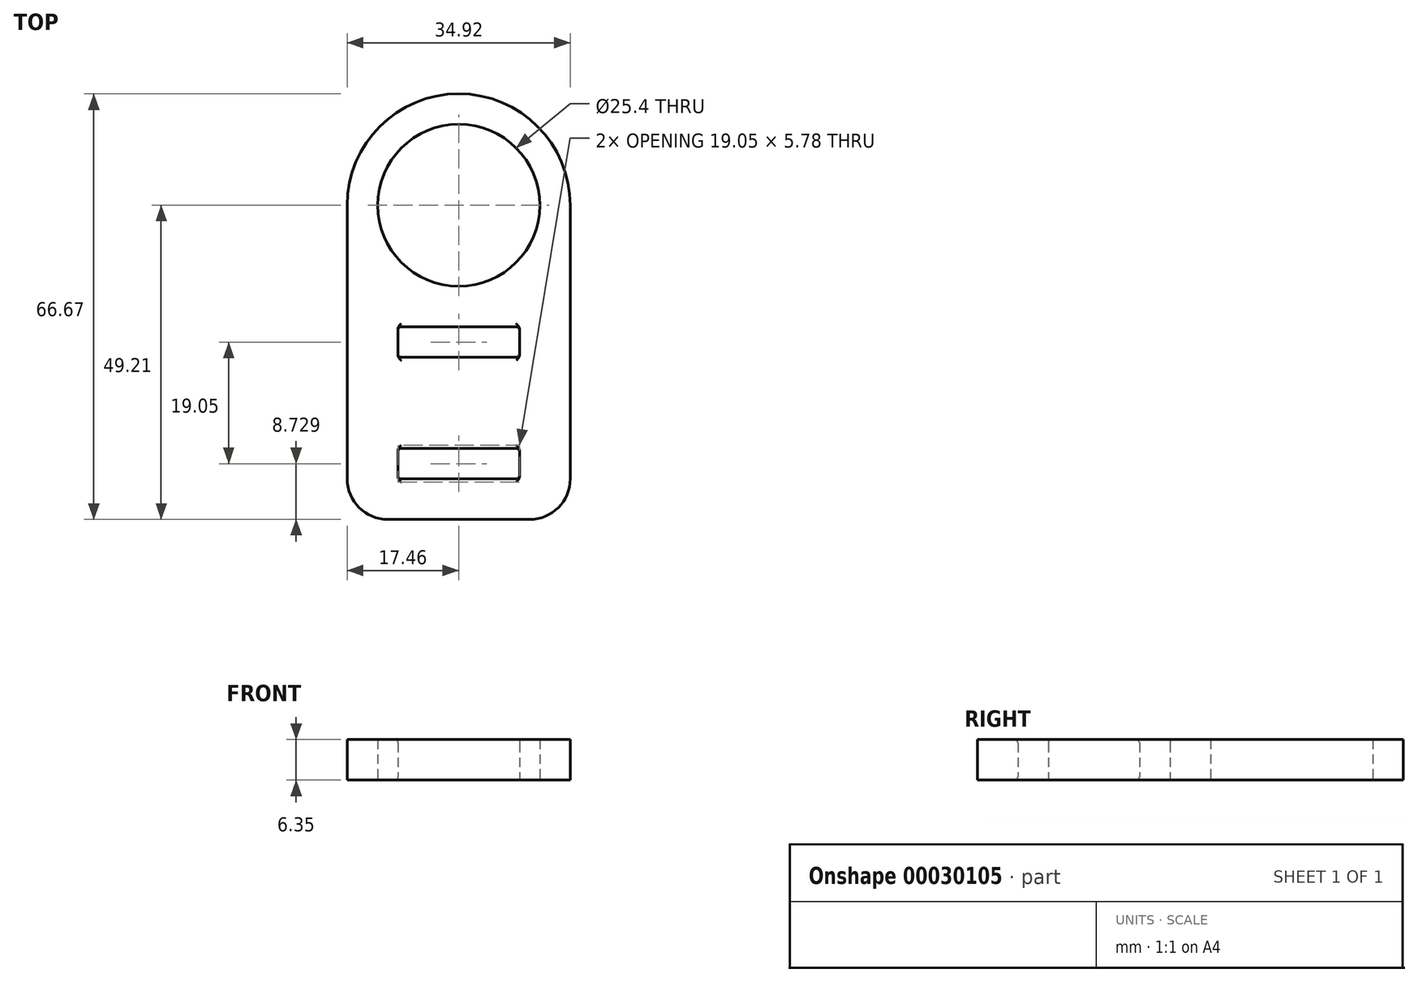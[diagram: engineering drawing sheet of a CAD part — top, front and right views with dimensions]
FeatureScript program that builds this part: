
annotation { "Feature Type Name" : "Feature", "Feature Type Description" : "" }
export const myFeature = defineFeature(function(context is Context, id is Id, definition is map)
    precondition{}
    {
        {
            var Q0;
            Q0=qCreatedBy(makeId("Top.planeOp"),FACE);
            var sketch = newSketch(context, id + "F0", { "sketchPlane" : qUnion([Q0])});
            skCircle(sketch, "E0", {"center": v(0, 0) * mm, "radius": 12.7 * mm});
            skArc(sketch, "E1", {"start": v(17.46, 0) * mm, "mid": v(0, 17.46) * mm, "end": v(-17.46, 0) * mm});
            skLineSegment(sketch, "E2", {"start": v(-17.46, 0) * mm, "end": v(-17.46, -42.86) * mm});
            skLineSegment(sketch, "E3", {"start": v(17.46, 0) * mm, "end": v(17.46, -42.86) * mm});
            skLineSegment(sketch, "E4", {"start": v(11.11, -49.21) * mm, "end": v(-11.11, -49.21) * mm});
            skLineSegment(sketch, "E5", {"start": v(0, 17.46) * mm, "end": v(0, -49.21) * mm, "construction": true});
            skPoint(sketch, "E6.visualSharp", {"position": v(-17.46, -49.21) * mm});
            skArc(sketch, "E6.filletArc", {"start": v(-17.46, -42.86) * mm, "mid": v(-15.6, -47.35) * mm, "end": v(-11.11, -49.21) * mm});
            skPoint(sketch, "E7.visualSharp", {"position": v(17.46, -49.21) * mm});
            skArc(sketch, "E7.filletArc", {"start": v(11.11, -49.21) * mm, "mid": v(15.6, -47.35) * mm, "end": v(17.46, -42.86) * mm});
            skLineSegment(sketch, "E8.rect.bottom", {"start": v(9.53, -38.1) * mm, "end": v(-9.52, -38.1) * mm});
            skLineSegment(sketch, "E8.rect.top", {"start": v(9.53, -42.86) * mm, "end": v(-9.52, -42.86) * mm});
            skLineSegment(sketch, "E8.rect.left", {"start": v(9.53, -38.1) * mm, "end": v(9.53, -42.86) * mm});
            skLineSegment(sketch, "E8.rect.right", {"start": v(-9.52, -38.1) * mm, "end": v(-9.52, -42.86) * mm});
            skPoint(sketch, "E8.rect.middle", {"position": v(0, -40.48) * mm});
            skLineSegment(sketch, "E9.0.1.0", {"start": v(9.53, -23.81) * mm, "end": v(-9.52, -23.81) * mm});
            skLineSegment(sketch, "E9.0.1.1", {"start": v(-9.52, -19.05) * mm, "end": v(-9.52, -23.81) * mm});
            skLineSegment(sketch, "E9.0.1.2", {"start": v(9.53, -19.05) * mm, "end": v(-9.52, -19.05) * mm});
            skLineSegment(sketch, "E9.0.1.3", {"start": v(9.53, -19.05) * mm, "end": v(9.53, -23.81) * mm});
            skLineSegment(sketch, "E9.direction1", {"start": v(-9.52, -42.86) * mm, "end": v(53.5, -42.86) * mm, "construction": true});
            skLineSegment(sketch, "E9.direction2", {"start": v(-9.52, -42.86) * mm, "end": v(-9.52, -23.81) * mm, "construction": true});
            skSolve(sketch);
        }
        {
            var Q0;
            Q0 = qSketchRegion(id + "F0", true);
            extrude(context, id + "F1", {"entities" : qUnion([Q0]), "depth" : 6.35 * mm});
        }
        {
            var Q0;
            Q0=makeQuery(id+"F1.opExtrude","CAP_EDGE",EDGE,{"disambiguationData":[OSD([sQuery(id+"F0.wireOp",EDGE,"E9.0.1.0")])],"isStart":false});
            var Q1;
            Q1=makeQuery(id+"F1.opExtrude","CAP_EDGE",EDGE,{"disambiguationData":[OSD([sQuery(id+"F0.wireOp",EDGE,"E9.0.1.0")])],"isStart":true});
            var Q2;
            Q2=makeQuery(id+"F1.opExtrude","CAP_EDGE",EDGE,{"disambiguationData":[OSD([sQuery(id+"F0.wireOp",EDGE,"E9.0.1.2")])],"isStart":false});
            var Q3;
            Q3=makeQuery(id+"F1.opExtrude","CAP_EDGE",EDGE,{"disambiguationData":[OSD([sQuery(id+"F0.wireOp",EDGE,"E8.rect.bottom")])],"isStart":false});
            var Q4;
            Q4=makeQuery(id+"F1.opExtrude","CAP_EDGE",EDGE,{"disambiguationData":[OSD([sQuery(id+"F0.wireOp",EDGE,"E8.rect.top")])],"isStart":false});
            var Q5;
            Q5=makeQuery(id+"F1.opExtrude","CAP_EDGE",EDGE,{"disambiguationData":[OSD([sQuery(id+"F0.wireOp",EDGE,"E8.rect.bottom")])],"isStart":true});
            var Q6;
            Q6=makeQuery(id+"F1.opExtrude","CAP_EDGE",EDGE,{"disambiguationData":[OSD([sQuery(id+"F0.wireOp",EDGE,"E9.0.1.2")])],"isStart":true});
            var Q7;
            Q7=makeQuery(id+"F1.opExtrude","CAP_EDGE",EDGE,{"disambiguationData":[OSD([sQuery(id+"F0.wireOp",EDGE,"E8.rect.top")])],"isStart":true});
            fillet(context, id + "F2", {"entities" : qUnion([Q0, Q1, Q2, Q3, Q4, Q5, Q6, Q7]), "radius" : 0.5 * mm, "tangentPropagation" : true, "allowEdgeOverflow" : false});
        }
        {
            var Q0;
            Q0=makeQuery(id+"F1.opExtrude","SWEPT_EDGE",EDGE,{"disambiguationData":[OSD([sQuery(id+"F0.wireOp",EDGE,"E8.rect.top"),sQuery(id+"F0.wireOp",EDGE,"E8.rect.left")])]});
            var Q1;
            Q1=makeQuery(id+"F1.opExtrude","SWEPT_EDGE",EDGE,{"disambiguationData":[OSD([sQuery(id+"F0.wireOp",EDGE,"E9.0.1.0"),sQuery(id+"F0.wireOp",EDGE,"E9.0.1.3")])]});
            var Q2;
            Q2=makeQuery(id+"F1.opExtrude","SWEPT_EDGE",EDGE,{"disambiguationData":[OSD([sQuery(id+"F0.wireOp",EDGE,"E8.rect.top"),sQuery(id+"F0.wireOp",EDGE,"E8.rect.right")])]});
            var Q3;
            Q3=makeQuery(id+"F1.opExtrude","SWEPT_EDGE",EDGE,{"disambiguationData":[OSD([sQuery(id+"F0.wireOp",EDGE,"E9.0.1.2"),sQuery(id+"F0.wireOp",EDGE,"E9.0.1.3")])]});
            var Q4;
            Q4=makeQuery(id+"F1.opExtrude","SWEPT_EDGE",EDGE,{"disambiguationData":[OSD([sQuery(id+"F0.wireOp",EDGE,"E9.0.1.1"),sQuery(id+"F0.wireOp",EDGE,"E9.0.1.2")])]});
            var Q5;
            Q5=makeQuery(id+"F1.opExtrude","SWEPT_EDGE",EDGE,{"disambiguationData":[OSD([sQuery(id+"F0.wireOp",EDGE,"E9.0.1.0"),sQuery(id+"F0.wireOp",EDGE,"E9.0.1.1")])]});
            var Q6;
            Q6=makeQuery(id+"F1.opExtrude","SWEPT_EDGE",EDGE,{"disambiguationData":[OSD([sQuery(id+"F0.wireOp",EDGE,"E8.rect.bottom"),sQuery(id+"F0.wireOp",EDGE,"E8.rect.right")])]});
            var Q7;
            Q7=makeQuery(id+"F1.opExtrude","SWEPT_EDGE",EDGE,{"disambiguationData":[OSD([sQuery(id+"F0.wireOp",EDGE,"E8.rect.bottom"),sQuery(id+"F0.wireOp",EDGE,"E8.rect.left")])]});
            fillet(context, id + "F3", {"entities" : qUnion([Q0, Q1, Q2, Q3, Q4, Q5, Q6, Q7]), "radius" : 0.5 * mm, "tangentPropagation" : true, "allowEdgeOverflow" : false});
        }
    });
